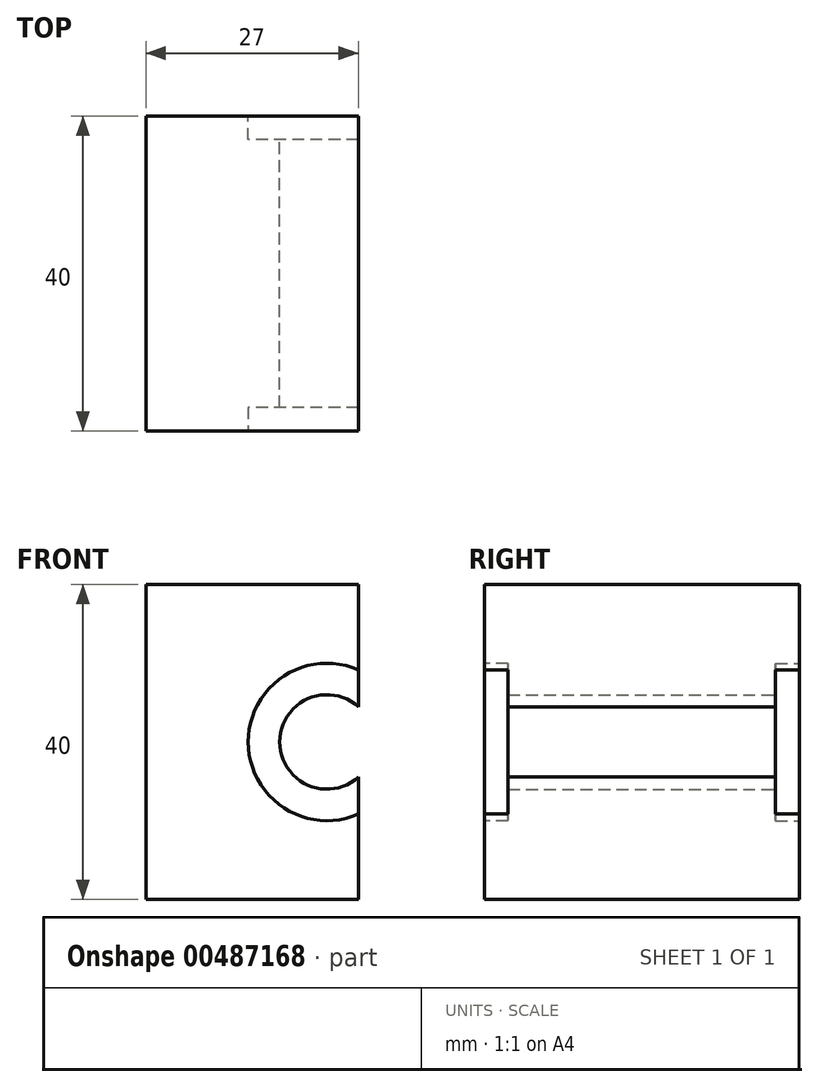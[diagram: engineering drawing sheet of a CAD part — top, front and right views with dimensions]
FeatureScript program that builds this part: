
annotation { "Feature Type Name" : "Feature", "Feature Type Description" : "" }
export const myFeature = defineFeature(function(context is Context, id is Id, definition is map)
    precondition{}
    {
        {
            var Q0;
            Q0=qCreatedBy(makeId("Front.planeOp"),FACE);
            var sketch = newSketch(context, id + "F0", { "sketchPlane" : qUnion([Q0])});
            skArc(sketch, "E0", {"start": v(4, 4.47) * mm, "mid": v(-6, 0) * mm, "end": v(4, -4.47) * mm});
            skLineSegment(sketch, "E1.bottom", {"start": v(4, 20) * mm, "end": v(-23, 20) * mm});
            skLineSegment(sketch, "E1.top", {"start": v(4, -20) * mm, "end": v(-23, -20) * mm});
            skLineSegment(sketch, "E1.left", {"start": v(4, 20) * mm, "end": v(4, 4.47) * mm});
            skLineSegment(sketch, "E1.right", {"start": v(-23, 20) * mm, "end": v(-23, -20) * mm});
            skLineSegment(sketch, "E2.trimOffspring", {"start": v(4, -4.47) * mm, "end": v(4, -20) * mm});
            skSolve(sketch);
        }
        {
            var Q0;
            Q0=makeQuery(id+"F0.imprint","IMPRINT",FACE,{"disambiguationData":[TD([[makeQuery(id+"F0.imprint","IMPRINT",EDGE,{"derivedFrom":sQuery(id+"F0.wireOp",EDGE,"E0")}),-1.0]])]});
            extrude(context, id + "F1", {"entities" : qUnion([Q0]), "depth" : 20 * mm, "hasSecondDirection" : true, "secondDirectionOppositeDirection" : true, "secondDirectionDepth" : 20 * mm});
        }
        {
            var Q0;
            Q0=makeQuery(id+"F1.opExtrude","CAP_FACE",FACE,{"disambiguationData":[OSD([sQuery(id+"F0.wireOp",EDGE,"E0"),sQuery(id+"F0.wireOp",EDGE,"E1.bottom"),sQuery(id+"F0.wireOp",EDGE,"E1.top"),sQuery(id+"F0.wireOp",EDGE,"E1.left"),sQuery(id+"F0.wireOp",EDGE,"E1.right"),sQuery(id+"F0.wireOp",EDGE,"E2.trimOffspring")])],"isStart":true});
            var sketch = newSketch(context, id + "F2", { "sketchPlane" : qUnion([Q0])});
            skCircle(sketch, "E3", {"center": v(0, 0) * mm, "radius": 10 * mm});
            skSolve(sketch);
        }
        {
            var Q0;
            Q0 = qSketchRegion(id + "F2", true);
            extrude(context, id + "F3", {"entities" : qUnion([Q0]), "operationType" : NewBodyOperationType.REMOVE, "oppositeDirection" : true, "depth" : 3 * mm});
        }
        {
            var Q0;
            Q0=makeQuery(id+"F1.opExtrude","CAP_FACE",FACE,{"disambiguationData":[OSD([sQuery(id+"F0.wireOp",EDGE,"E0"),sQuery(id+"F0.wireOp",EDGE,"E1.bottom"),sQuery(id+"F0.wireOp",EDGE,"E1.top"),sQuery(id+"F0.wireOp",EDGE,"E1.left"),sQuery(id+"F0.wireOp",EDGE,"E1.right"),sQuery(id+"F0.wireOp",EDGE,"E2.trimOffspring")])],"isStart":false});
            var sketch = newSketch(context, id + "F4", { "sketchPlane" : qUnion([Q0])});
            skCircle(sketch, "E4", {"center": v(0, 0) * mm, "radius": 10 * mm});
            skSolve(sketch);
        }
        {
            var Q0;
            Q0 = qSketchRegion(id + "F4", true);
            extrude(context, id + "F5", {"entities" : qUnion([Q0]), "operationType" : NewBodyOperationType.REMOVE, "oppositeDirection" : true, "depth" : 3 * mm});
        }
    });
